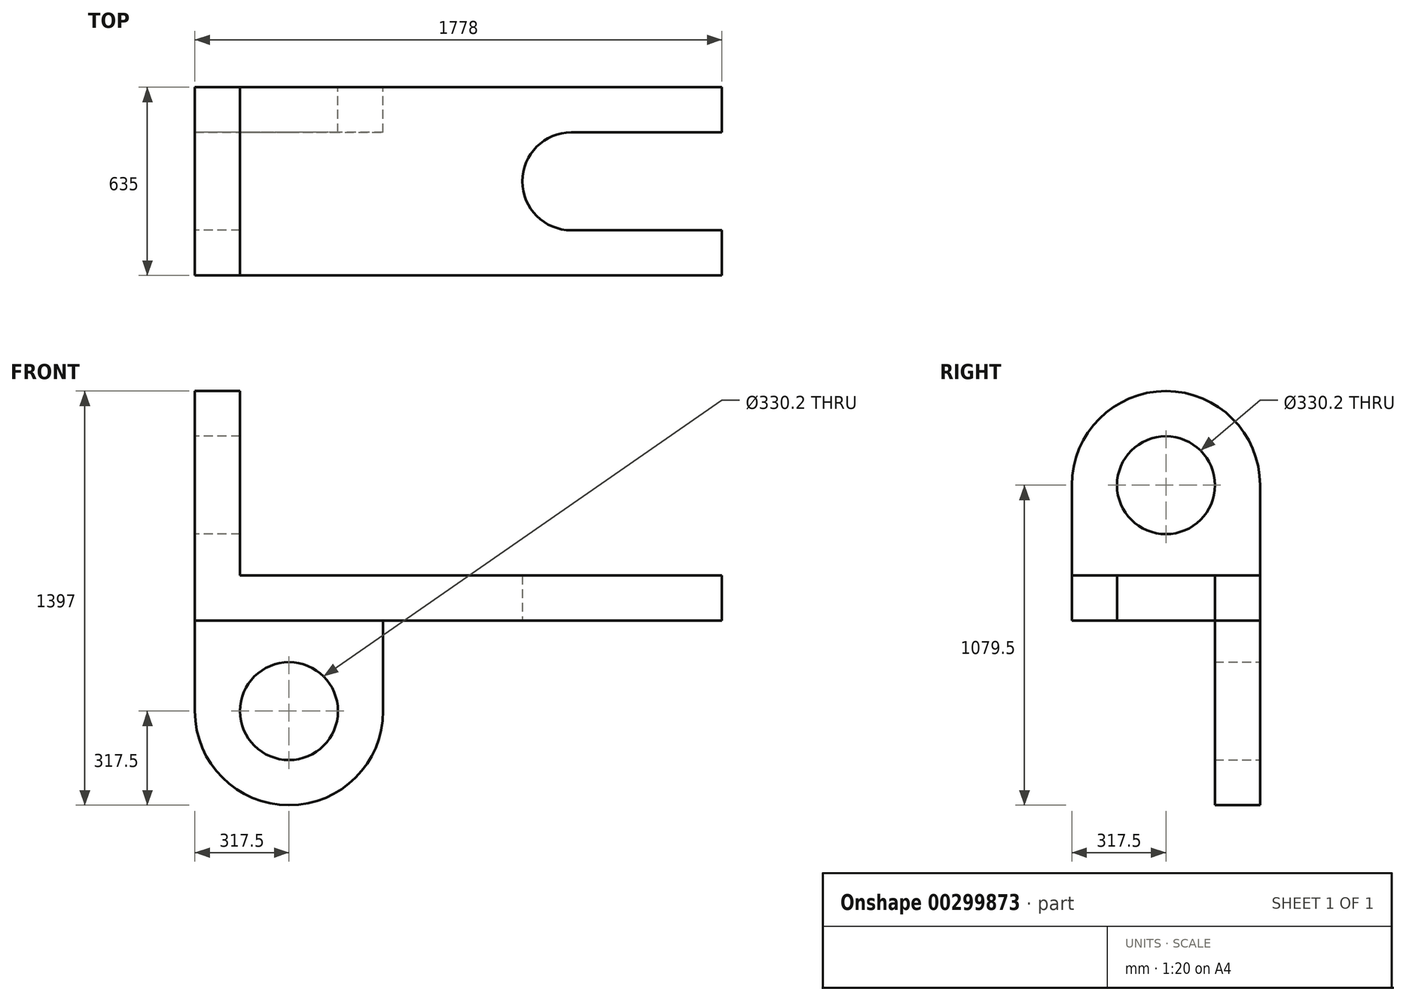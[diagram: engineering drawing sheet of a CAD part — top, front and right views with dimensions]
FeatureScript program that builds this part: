
annotation { "Feature Type Name" : "Feature", "Feature Type Description" : "" }
export const myFeature = defineFeature(function(context is Context, id is Id, definition is map)
    precondition{}
    {
        {
            var Q0;
            Q0=qCreatedBy(makeId("Top.planeOp"),FACE);
            var sketch = newSketch(context, id + "F0", { "sketchPlane" : qUnion([Q0])});
            skLineSegment(sketch, "E0.bottom", {"start": v(0, -317.5) * mm, "end": v(1778, -317.5) * mm});
            skLineSegment(sketch, "E0.top", {"start": v(0, 317.5) * mm, "end": v(1778, 317.5) * mm});
            skLineSegment(sketch, "E1", {"start": v(0, 317.5) * mm, "end": v(0, -317.5) * mm});
            skLineSegment(sketch, "E2", {"start": v(1778, 317.5) * mm, "end": v(1778, 165.1) * mm});
            skLineSegment(sketch, "E3", {"start": v(1778, 165.1) * mm, "end": v(1270, 165.1) * mm});
            skArc(sketch, "E4", {"start": v(1270, 165.1) * mm, "mid": v(1104.9, 0) * mm, "end": v(1270, -165.1) * mm});
            skLineSegment(sketch, "E5", {"start": v(1270, -165.1) * mm, "end": v(1778, -165.1) * mm});
            skLineSegment(sketch, "E6", {"start": v(1778, -165.1) * mm, "end": v(1778, -317.5) * mm});
            skSolve(sketch);
        }
        {
            var Q0;
            Q0 = qSketchRegion(id + "F0", true);
            extrude(context, id + "F1", {"entities" : qUnion([Q0]), "depth" : 152.4 * mm});
        }
        {
            var Q0;
            Q0=makeQuery(id+"F1.opExtrude","SWEPT_FACE",FACE,{"disambiguationData":[OSD([sQuery(id+"F0.wireOp",EDGE,"E1")])]});
            var sketch = newSketch(context, id + "F2", { "sketchPlane" : qUnion([Q0])});
            skCircle(sketch, "E7", {"center": v(0, 457.2) * mm, "radius": 165.1 * mm});
            skLineSegment(sketch, "E8", {"start": v(-317.5, 152.4) * mm, "end": v(-317.5, 457.2) * mm});
            skLineSegment(sketch, "E9", {"start": v(317.5, 152.4) * mm, "end": v(317.5, 457.2) * mm});
            skArc(sketch, "E10", {"start": v(-317.5, 457.2) * mm, "mid": v(0, 774.7) * mm, "end": v(317.5, 457.2) * mm});
            skLineSegment(sketch, "E11", {"start": v(-317.5, 152.4) * mm, "end": v(317.5, 152.4) * mm});
            skSolve(sketch);
        }
        {
            var Q0;
            Q0 = qSketchRegion(id + "F2", true);
            extrude(context, id + "F3", {"entities" : qUnion([Q0]), "operationType" : NewBodyOperationType.ADD, "oppositeDirection" : true, "depth" : 152.4 * mm});
        }
        {
            var Q0;
            Q0=makeQuery(id+"F3.boolean.opBoolean","MERGE",FACE,{"derivedFrom":[makeQuery(id+"F1.opExtrude","SWEPT_FACE",FACE,{"disambiguationData":[OSD([sQuery(id+"F0.wireOp",EDGE,"E0.top")])]}),makeQuery(id+"F3.opExtrude","SWEPT_FACE",FACE,{"disambiguationData":[OSD([sQuery(id+"F2.wireOp",EDGE,"E8")])]})]});
            var sketch = newSketch(context, id + "F4", { "sketchPlane" : qUnion([Q0])});
            skLineSegment(sketch, "E12", {"start": v(0, 0) * mm, "end": v(-635, 0) * mm});
            skLineSegment(sketch, "E13", {"start": v(0, 0) * mm, "end": v(0, -304.8) * mm});
            skLineSegment(sketch, "E14", {"start": v(-635, 0) * mm, "end": v(-635, -304.8) * mm});
            skArc(sketch, "E15", {"start": v(0, -304.8) * mm, "mid": v(-317.5, -622.3) * mm, "end": v(-635, -304.8) * mm});
            skCircle(sketch, "E16", {"center": v(-317.5, -304.8) * mm, "radius": 165.1 * mm});
            skSolve(sketch);
        }
        {
            var Q0;
            Q0 = qSketchRegion(id + "F4", true);
            extrude(context, id + "F5", {"entities" : qUnion([Q0]), "operationType" : NewBodyOperationType.ADD, "oppositeDirection" : true, "depth" : 152.4 * mm});
        }
    });
